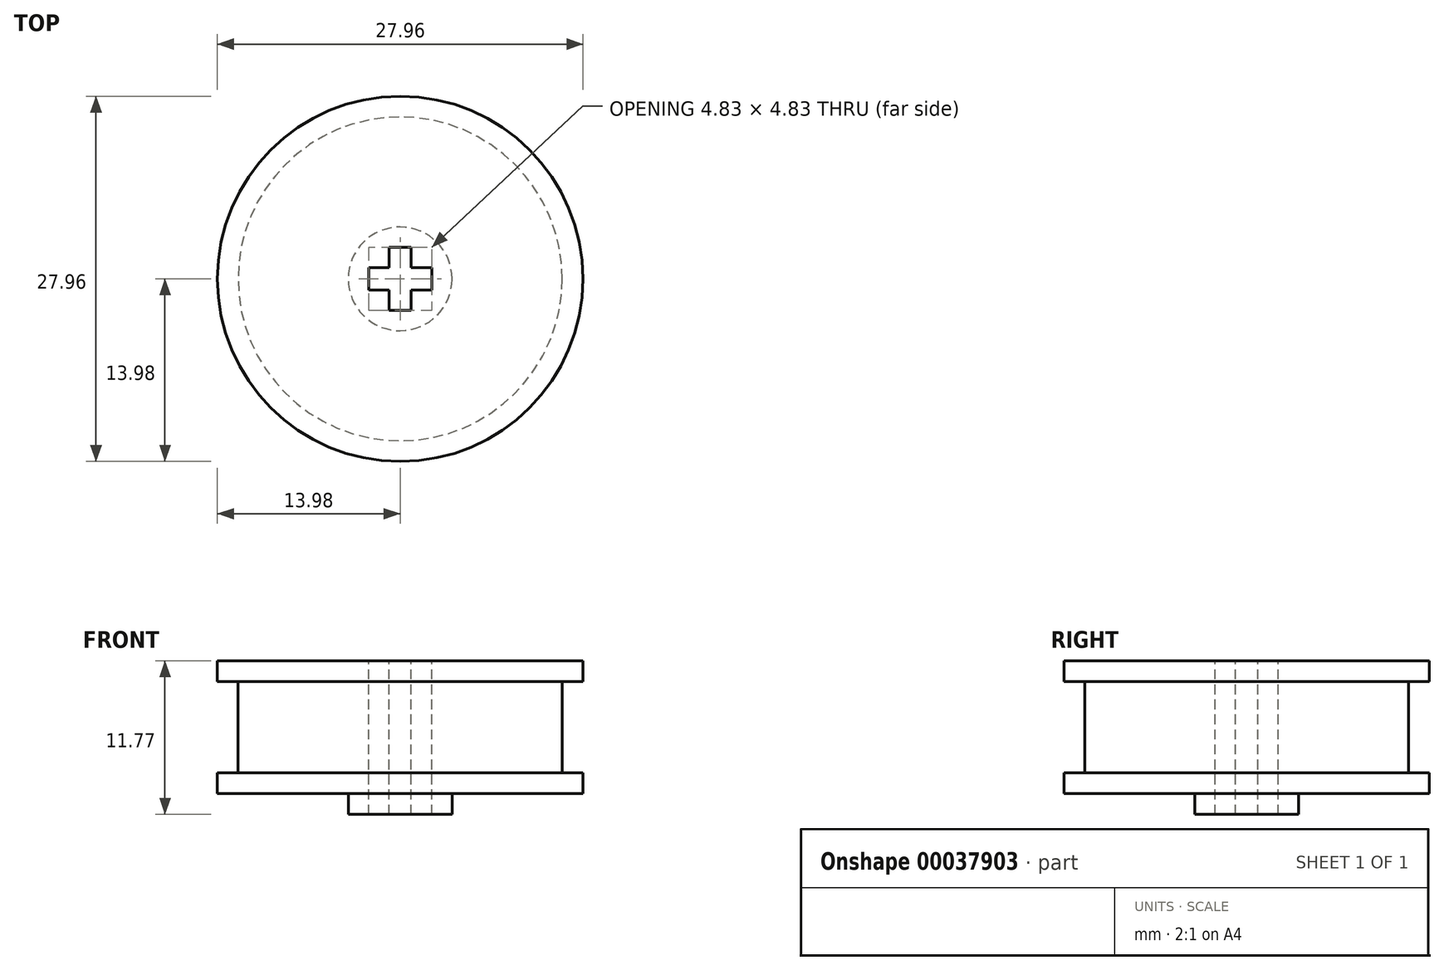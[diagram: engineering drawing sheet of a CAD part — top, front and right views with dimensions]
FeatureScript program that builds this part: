
annotation { "Feature Type Name" : "Feature", "Feature Type Description" : "" }
export const myFeature = defineFeature(function(context is Context, id is Id, definition is map)
    precondition{}
    {
        {
            var Q0;
            Q0=qCreatedBy(makeId("Top.planeOp"),FACE);
            var sketch = newSketch(context, id + "F0", { "sketchPlane" : qUnion([Q0])});
            skCircle(sketch, "E0", {"center": v(0, 0) * mm, "radius": 13.98 * mm});
            skSolve(sketch);
        }
        {
            var Q0;
            Q0 = qSketchRegion(id + "F0", true);
            extrude(context, id + "F1", {"entities" : qUnion([Q0]), "depth" : 1.59 * mm});
        }
        {
            var Q0;
            Q0=makeQuery(id+"F1.opExtrude","CAP_FACE",FACE,{"disambiguationData":[OSD([sQuery(id+"F0.wireOp",EDGE,"E0")])],"isStart":false});
            var sketch = newSketch(context, id + "F2", { "sketchPlane" : qUnion([Q0])});
            skCircle(sketch, "E1", {"center": v(0, 0) * mm, "radius": 12.4 * mm});
            skSolve(sketch);
        }
        {
            var Q0;
            Q0 = qSketchRegion(id + "F2", true);
            extrude(context, id + "F3", {"entities" : qUnion([Q0]), "operationType" : NewBodyOperationType.ADD, "depth" : 7 * mm});
        }
        {
            var Q0;
            Q0=makeQuery(id+"F3.opExtrude","CAP_FACE",FACE,{"disambiguationData":[OSD([sQuery(id+"F2.wireOp",EDGE,"E1")])],"isStart":false});
            var sketch = newSketch(context, id + "F4", { "sketchPlane" : qUnion([Q0])});
            skCircle(sketch, "E2", {"center": v(0, 0) * mm, "radius": 13.98 * mm});
            skSolve(sketch);
        }
        {
            var Q0;
            Q0 = qSketchRegion(id + "F4", true);
            extrude(context, id + "F5", {"entities" : qUnion([Q0]), "operationType" : NewBodyOperationType.ADD, "depth" : 1.59 * mm});
        }
        {
            var Q0;
            Q0=makeQuery(id+"F1.opExtrude","CAP_FACE",FACE,{"disambiguationData":[OSD([sQuery(id+"F0.wireOp",EDGE,"E0")])],"isStart":true});
            var sketch = newSketch(context, id + "F6", { "sketchPlane" : qUnion([Q0])});
            skCircle(sketch, "E3", {"center": v(0, 0) * mm, "radius": 3.97 * mm});
            skSolve(sketch);
        }
        {
            var Q0;
            Q0 = qSketchRegion(id + "F6", true);
            extrude(context, id + "F7", {"entities" : qUnion([Q0]), "operationType" : NewBodyOperationType.ADD, "depth" : 1.59 * mm});
        }
        {
            var Q0;
            Q0=makeQuery(id+"F5.opExtrude","CAP_FACE",FACE,{"disambiguationData":[OSD([sQuery(id+"F4.wireOp",EDGE,"E2")])],"isStart":false});
            var sketch = newSketch(context, id + "F8", { "sketchPlane" : qUnion([Q0])});
            skLineSegment(sketch, "E4.rect.bottom", {"start": v(2.41, -0.84) * mm, "end": v(-2.41, -0.84) * mm});
            skLineSegment(sketch, "E4.rect.top", {"start": v(2.41, 0.84) * mm, "end": v(-2.41, 0.84) * mm});
            skLineSegment(sketch, "E4.rect.left", {"start": v(2.41, -0.84) * mm, "end": v(2.41, 0.84) * mm});
            skLineSegment(sketch, "E4.rect.right", {"start": v(-2.41, -0.84) * mm, "end": v(-2.41, 0.84) * mm});
            skPoint(sketch, "E4.rect.middle", {"position": v(0, 0) * mm});
            skLineSegment(sketch, "E5.rect.bottom", {"start": v(0.84, -2.41) * mm, "end": v(-0.84, -2.41) * mm});
            skLineSegment(sketch, "E5.rect.top", {"start": v(0.84, 2.41) * mm, "end": v(-0.84, 2.41) * mm});
            skLineSegment(sketch, "E5.rect.left", {"start": v(0.84, -2.41) * mm, "end": v(0.84, 2.41) * mm});
            skLineSegment(sketch, "E5.rect.right", {"start": v(-0.84, -2.41) * mm, "end": v(-0.84, 2.41) * mm});
            skSolve(sketch);
        }
        {
            var Q0;
            Q0 = qSketchRegion(id + "F8", true);
            var Q1;
            Q1=makeQuery(id+"F7.opExtrude","CAP_FACE",FACE,{"disambiguationData":[OSD([sQuery(id+"F6.wireOp",EDGE,"E3")])],"isStart":false});
            extrude(context, id + "F9", {"entities" : qUnion([Q0]), "operationType" : NewBodyOperationType.REMOVE, "endBound" : BoundingType.UP_TO_SURFACE, "oppositeDirection" : true, "endBoundEntityFace" : qUnion([Q1]), "depth" : 25.4 * mm});
        }
    });
